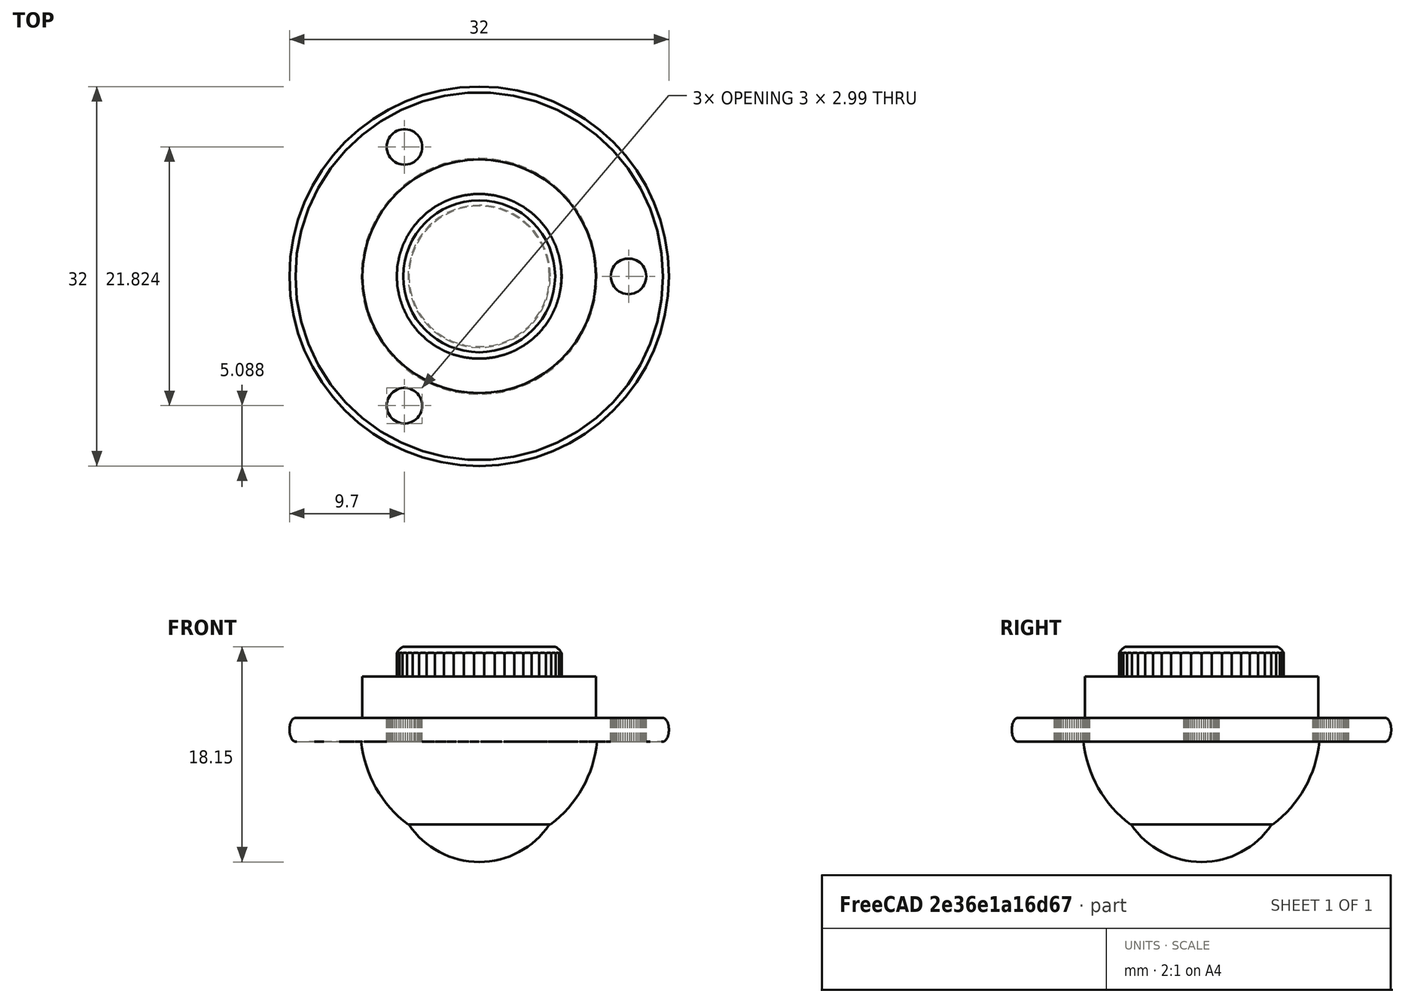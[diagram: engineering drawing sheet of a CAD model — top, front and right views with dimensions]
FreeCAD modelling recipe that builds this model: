
FCSTD DOCUMENT  (FreeCAD 0.16R6707 (Git))
Label: bille_scad
License: All rights reserved
LicenseURL: http://en.wikipedia.org/wiki/All_rights_reserved
objects: Part::Prism×5, Part::Cut×4, Part::Part2DObjectPython×3, Part::FeaturePython×3, Part::Revolution×2, Part::Fuse×2, Part::MultiFuse×2, Part::Box×2, Part::Feature×1, Part::Extrusion×1, Part::Plane×1, Part::Sphere×1
note: 27 computed .brp shape members not serialized (recipe doc carries the construction recipe); baked Part::Feature solids carry a one-line shape summary decoded from their .brp

FEATURE [Part::Prism] prism
  Circumradius = 15.5
  Height = 2
  Placement = pos=(0,0,-1) rot=(0,0,1;0rad)
  Polygon = 50
FEATURE [Part::Part2DObjectPython] circle  # Draft 2D object (typed FeaturePython)
  FirstAngle = 0
  LastAngle = 0
  MakeFace = true
  Placement = pos=(31,0,0) rot=(0,0,1;0rad)
  Radius = 1
FEATURE [Part::Feature] Matrix_Deformation
  Placement = pos=(31,0,0) rot=(0,0,1;0rad)
  shape: bbox 1 x 2 x 2e-07 mm, 1 faces, 0 solids (baked)
FEATURE [Part::FeaturePython] RefineRotateExtrude  # WARN: FeaturePython — macro-defined, semantics opaque (R4)
  Base = -> Matrix_Deformation
FEATURE [Part::Revolution] RotateExtrude
  Angle = 360
  Axis = (0,1,0)
  Base = (0,0,0)
  Placement = pos=(0,0,0) rot=(1,0,0;1.5708rad)
  Solid = false
  Source = -> RefineRotateExtrude
FEATURE [Part::Fuse] union
  Base = -> prism
  Tool = -> RotateExtrude
FEATURE [Part::Prism] prism001
  Circumradius = 1.5
  Height = 3
  Placement = pos=(12.6,0,-1.5) rot=(0,0,1;0rad)
  Polygon = 50
FEATURE [Part::Prism] prism002
  Circumradius = 1.5
  Height = 3
  Placement = pos=(-6.3,10.9119,-1.5) rot=(0,0,1;0rad)
  Polygon = 50
FEATURE [Part::Prism] prism003
  Circumradius = 1.5
  Height = 3
  Placement = pos=(-6.3,-10.9119,-1.5) rot=(0,0,1;0rad)
  Polygon = 50
FEATURE [Part::MultiFuse] Group
  Shapes = -> [prism001,prism002,prism003]
FEATURE [Part::Cut] difference
  Base = -> union
  Tool = -> Group
FEATURE [Part::Part2DObjectPython] circle001  # Draft 2D object (typed FeaturePython)
  FirstAngle = 0
  LastAngle = 0
  MakeFace = true
  Radius = 9.85
FEATURE [Part::FeaturePython] RefineLinearExtrude  # WARN: FeaturePython — macro-defined, semantics opaque (R4)
  Base = -> circle001
FEATURE [Part::Extrusion] LinearExtrude
  Base = -> RefineLinearExtrude
  Dir = (0,0,3.5)
  Placement = pos=(0,0,1) rot=(0,0,1;0rad)
  Solid = true
FEATURE [Part::Prism] prism004
  Circumradius = 6.95
  Height = 2.5
  Placement = pos=(0,0,-1.25) rot=(0,0,1;0rad)
  Polygon = 50
FEATURE [Part::Plane] square
  Length = 1.1
  Placement = pos=(5.9,-0.55,0) rot=(0,0,1;0rad)
  Width = 1.1
FEATURE [Part::Part2DObjectPython] circle002  # Draft 2D object (typed FeaturePython)
  FirstAngle = 0
  LastAngle = 0
  MakeFace = true
  Placement = pos=(5.95,-0.5,0) rot=(0,0,1;0rad)
  Radius = 1.1
FEATURE [Part::Cut] difference001
  Base = -> square
  Tool = -> circle002
FEATURE [Part::FeaturePython] RefineRotateExtrude001  # WARN: FeaturePython — macro-defined, semantics opaque (R4)
  Base = -> difference001
FEATURE [Part::Revolution] RotateExtrude001
  Angle = 360
  Axis = (0,1,0)
  Base = (0,0,0)
  Placement = pos=(0,0,0.75) rot=(1,0,0;1.5708rad)
  Solid = false
  Source = -> RefineRotateExtrude001
FEATURE [Part::Cut] difference002
  Base = -> prism004
  Placement = pos=(0,0,5.75) rot=(0,0,1;0rad)
  Tool = -> RotateExtrude001
FEATURE [Part::Sphere] sphere
  Angle1 = -90
  Angle2 = 90
  Angle3 = 360
  Radius = 10
FEATURE [Part::Box] cube
  Height = 20
  Length = 20
  Placement = pos=(-10,-10,0) rot=(0,0,1;0rad)
  Width = 20
FEATURE [Part::Box] cube001
  Height = 20
  Length = 20
  Placement = pos=(-10,-10,-28) rot=(0,0,1;0rad)
  Width = 20
FEATURE [Part::Fuse] union001
  Base = -> cube
  Tool = -> cube001
FEATURE [Part::Cut] difference003
  Base = -> sphere
  Tool = -> union001
FEATURE [Part::MultiFuse] Group001
  Shapes = -> [difference,LinearExtrude,difference002,difference003]
